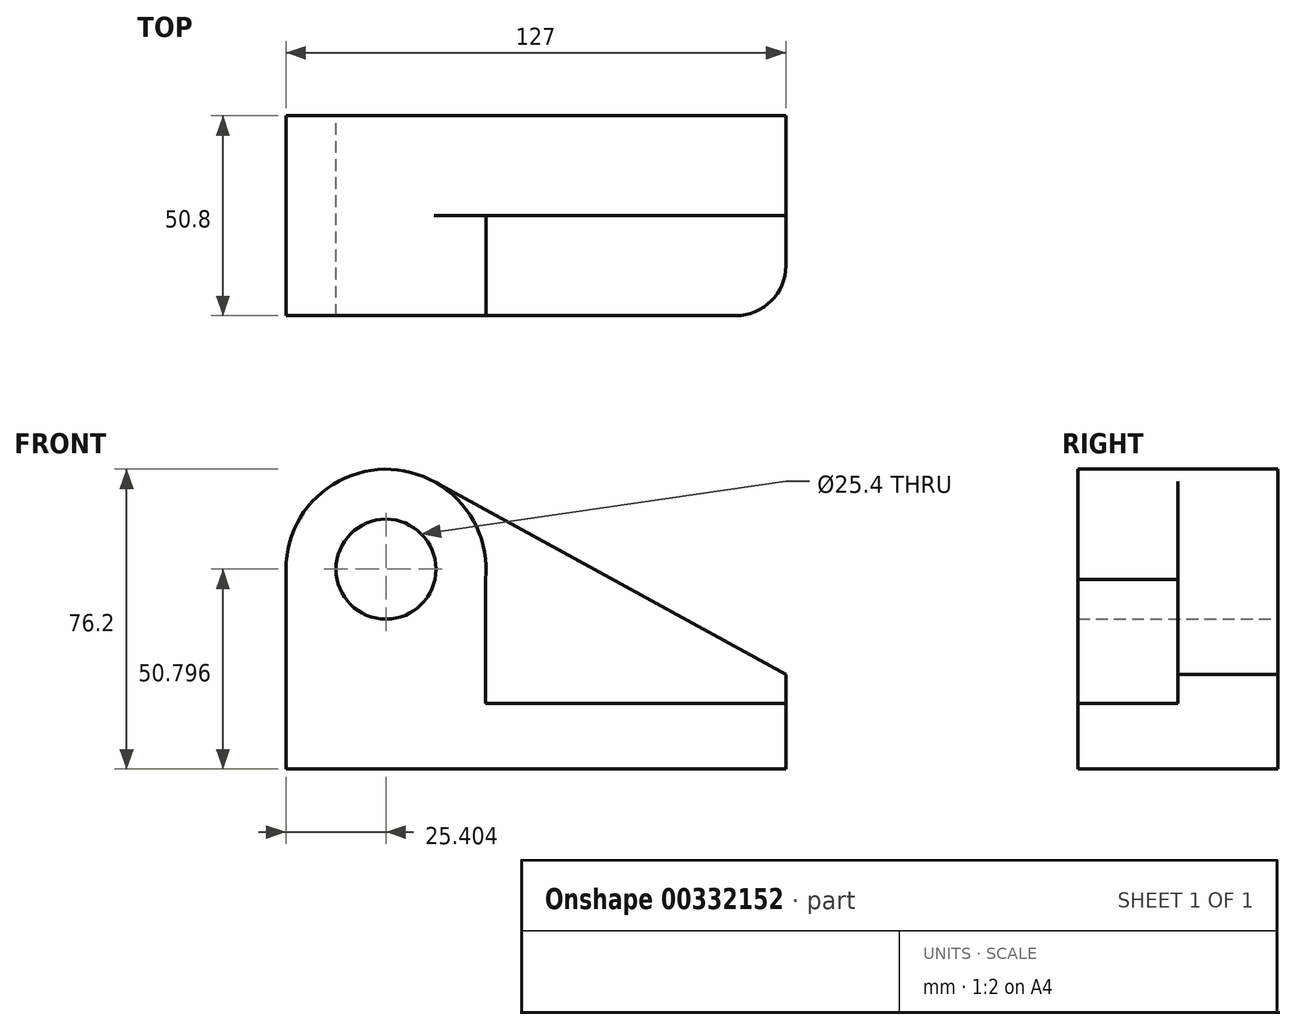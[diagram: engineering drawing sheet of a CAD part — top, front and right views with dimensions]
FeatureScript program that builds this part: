
annotation { "Feature Type Name" : "Feature", "Feature Type Description" : "" }
export const myFeature = defineFeature(function(context is Context, id is Id, definition is map)
    precondition{}
    {
        {
            var Q0;
            Q0=qCreatedBy(makeId("Front.planeOp"),FACE);
            var sketch = newSketch(context, id + "F0", { "sketchPlane" : qUnion([Q0])});
            skCircle(sketch, "E0", {"center": v(-42.68, 15.16) * mm, "radius": 12.7 * mm});
            skArc(sketch, "E1", {"start": v(-30.46, 37.43) * mm, "mid": v(-55.62, 37.01) * mm, "end": v(-68.08, 15.16) * mm});
            skLineSegment(sketch, "E2", {"start": v(-68.08, 15.16) * mm, "end": v(-68.08, -35.64) * mm});
            skLineSegment(sketch, "E3", {"start": v(-68.08, -35.64) * mm, "end": v(58.92, -35.64) * mm});
            skLineSegment(sketch, "E4", {"start": v(58.92, -35.64) * mm, "end": v(58.92, -21.58) * mm});
            skLineSegment(sketch, "E5", {"start": v(58.92, -21.58) * mm, "end": v(58.92, -11.59) * mm});
            skLineSegment(sketch, "E6", {"start": v(58.92, -11.59) * mm, "end": v(46.22, -11.59) * mm});
            skLineSegment(sketch, "E7", {"start": v(58.92, -11.59) * mm, "end": v(-30.46, 37.43) * mm});
            skSolve(sketch);
        }
        {
            var Q0;
            Q0=makeQuery(id+"F0.imprint","IMPRINT",FACE,{"disambiguationData":[TD([[makeQuery(id+"F0.imprint","IMPRINT",EDGE,{"derivedFrom":sQuery(id+"F0.wireOp",EDGE,"E0")}),-1.0]])]});
            extrude(context, id + "F1", {"entities" : qUnion([Q0]), "depth" : 25.4 * mm});
        }
        {
            var Q0;
            Q0=makeQuery(id+"F1.opExtrude","CAP_FACE",FACE,{"disambiguationData":[OSD([sQuery(id+"F0.wireOp",EDGE,"E0"),sQuery(id+"F0.wireOp",EDGE,"E1"),sQuery(id+"F0.wireOp",EDGE,"E2"),sQuery(id+"F0.wireOp",EDGE,"E3"),sQuery(id+"F0.wireOp",EDGE,"E4"),sQuery(id+"F0.wireOp",EDGE,"E5"),sQuery(id+"F0.wireOp",EDGE,"E7")])],"isStart":false});
            cPlane(context, id + "F2", {"entities" : qUnion([Q0]), "cplaneType" : CPlaneType.OFFSET, "offset" : 25.4 * mm, "width" : 152.4 * mm, "height" : 152.4 * mm});
        }
        {
            var Q0;
            Q0=qCreatedBy(id+"F2.planeOp",FACE);
            var sketch = newSketch(context, id + "F3", { "sketchPlane" : qUnion([Q0])});
            skSolve(sketch);
        }
        {
            var Q0;
            Q0=makeQuery(id+"F1.opExtrude","CAP_FACE",FACE,{"disambiguationData":[OSD([sQuery(id+"F0.wireOp",EDGE,"E0"),sQuery(id+"F0.wireOp",EDGE,"E1"),sQuery(id+"F0.wireOp",EDGE,"E2"),sQuery(id+"F0.wireOp",EDGE,"E3"),sQuery(id+"F0.wireOp",EDGE,"E4"),sQuery(id+"F0.wireOp",EDGE,"E5"),sQuery(id+"F0.wireOp",EDGE,"E7")])],"isStart":false});
            var sketch = newSketch(context, id + "F4", { "sketchPlane" : qUnion([Q0])});
            skCircle(sketch, "E8", {"center": v(-42.68, 15.16) * mm, "radius": 12.7 * mm});
            skArc(sketch, "E9", {"start": v(-17.4, 12.58) * mm, "mid": v(-41.39, 40.52) * mm, "end": v(-68.08, 15.16) * mm});
            skLineSegment(sketch, "E10.bottom", {"start": v(-68.08, -35.64) * mm, "end": v(58.92, -35.64) * mm});
            skLineSegment(sketch, "E10.top", {"start": v(-17.4, -19) * mm, "end": v(58.92, -19) * mm});
            skLineSegment(sketch, "E10.left", {"start": v(-68.08, -35.64) * mm, "end": v(-68.08, -19) * mm});
            skLineSegment(sketch, "E10.right", {"start": v(58.92, -35.64) * mm, "end": v(58.92, -19) * mm});
            skLineSegment(sketch, "E11", {"start": v(-17.4, 12.58) * mm, "end": v(-17.4, -19) * mm});
            skSolve(sketch);
        }
        {
            var Q0;
            Q0=makeQuery(id+"F4.imprint","IMPRINT",FACE,{"disambiguationData":[TD([[makeQuery(id+"F4.imprint","IMPRINT",EDGE,{"derivedFrom":sQuery(id+"F4.wireOp",EDGE,"E8")}),-1.0]])]});
            extrude(context, id + "F5", {"entities" : qUnion([Q0]), "operationType" : NewBodyOperationType.ADD, "depth" : 25.4 * mm});
        }
        {
            var Q0;
            Q0=makeQuery(id+"F5.opExtrude","CAP_EDGE",EDGE,{"disambiguationData":[OSD([sQuery(id+"F4.wireOp",EDGE,"E10.right")])],"isStart":false});
            fillet(context, id + "F6", {"entities" : qUnion([Q0]), "radius" : 12.7 * mm, "tangentPropagation" : true, "allowEdgeOverflow" : false});
        }
    });
